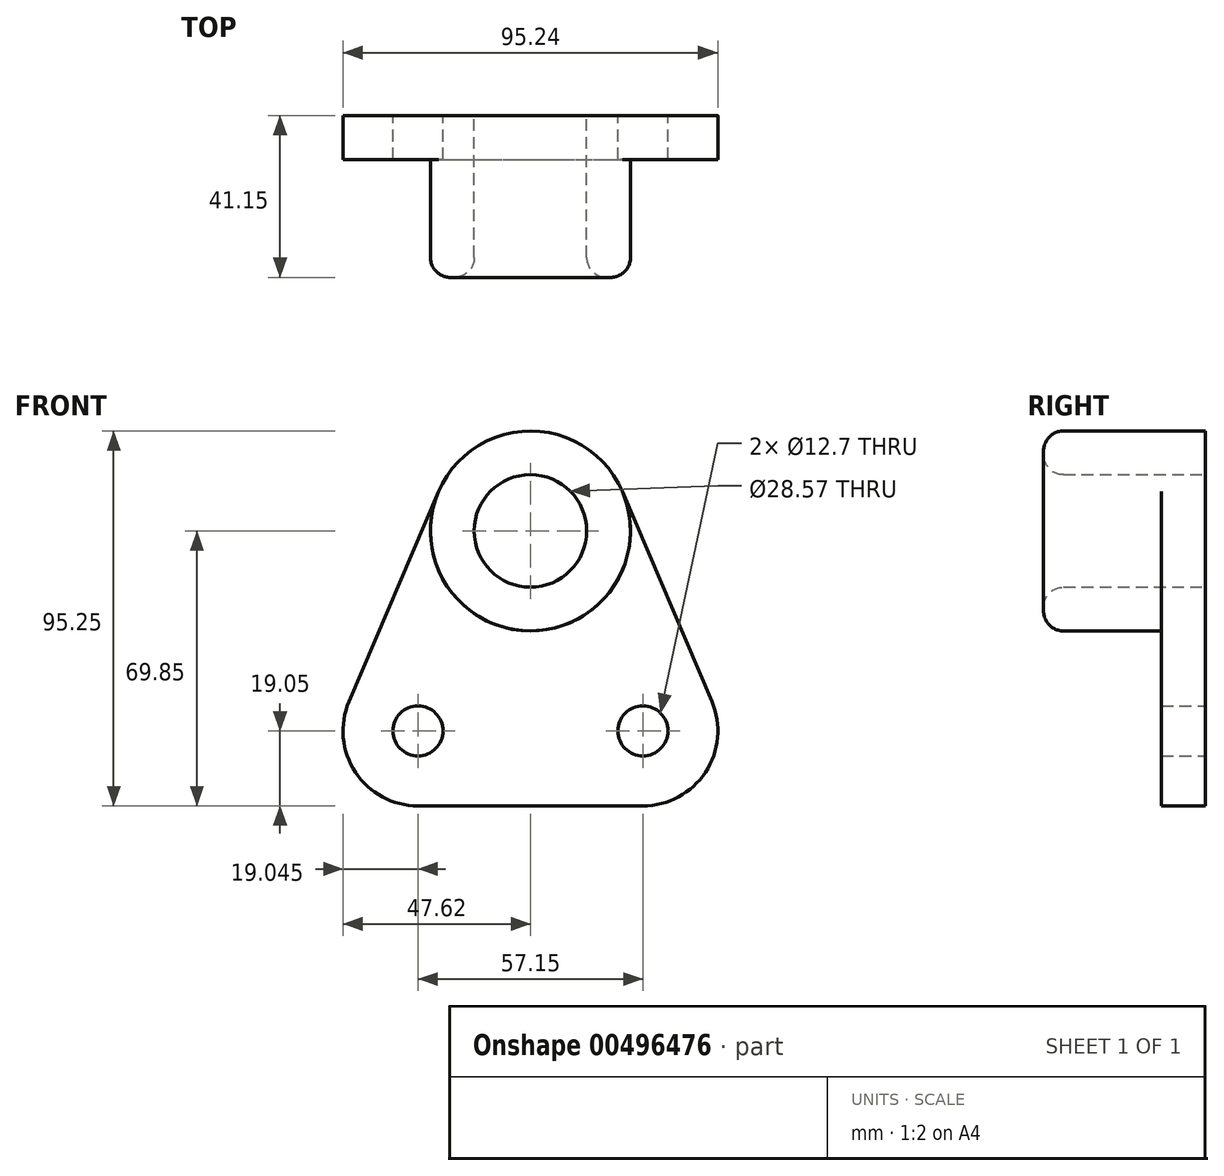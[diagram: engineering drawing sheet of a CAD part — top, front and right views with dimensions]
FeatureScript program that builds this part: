
annotation { "Feature Type Name" : "Feature", "Feature Type Description" : "" }
export const myFeature = defineFeature(function(context is Context, id is Id, definition is map)
    precondition{}
    {
        {
            var Q0;
            Q0=qCreatedBy(makeId("Front.planeOp"),FACE);
            var sketch = newSketch(context, id + "F0", { "sketchPlane" : qUnion([Q0])});
            skCircle(sketch, "E0", {"center": v(0, 0) * mm, "radius": 14.29 * mm});
            skCircle(sketch, "E1", {"center": v(0, 0) * mm, "radius": 25.4 * mm});
            skCircle(sketch, "E2", {"center": v(-28.57, -50.8) * mm, "radius": 19.05 * mm});
            skCircle(sketch, "E3", {"center": v(28.58, -50.8) * mm, "radius": 19.05 * mm});
            skCircle(sketch, "E4", {"center": v(28.58, -50.8) * mm, "radius": 6.35 * mm});
            skCircle(sketch, "E5", {"center": v(-28.57, -50.8) * mm, "radius": 6.35 * mm});
            skLineSegment(sketch, "E6", {"start": v(-23.36, 9.97) * mm, "end": v(-46.1, -43.33) * mm});
            skLineSegment(sketch, "E7", {"start": v(-28.58, -69.85) * mm, "end": v(28.58, -69.85) * mm});
            skLineSegment(sketch, "E8", {"start": v(46.1, -43.33) * mm, "end": v(23.36, 9.97) * mm});
            skLineSegment(sketch, "E9", {"start": v(-28.58, -50.8) * mm, "end": v(0, -50.8) * mm, "construction": true});
            skLineSegment(sketch, "E10", {"start": v(0, -50.8) * mm, "end": v(28.58, -50.8) * mm, "construction": true});
            skSolve(sketch);
        }
        {
            var Q0;
            Q0=makeQuery(id+"F0.imprint","IMPRINT",FACE,{"disambiguationData":[TD([[makeQuery(id+"F0.imprint","IMPRINT",EDGE,{"derivedFrom":sQuery(id+"F0.wireOp",EDGE,"E0")}),-1.0]])]});
            extrude(context, id + "F1", {"entities" : qUnion([Q0]), "depth" : 41.15 * mm, "offsetDistance" : 25.4 * mm});
        }
        {
            var Q0;
            Q0=makeQuery(id+"F1.opExtrude","CAP_FACE",FACE,{"disambiguationData":[OSD([sQuery(id+"F0.wireOp",EDGE,"E0"),sQuery(id+"F0.wireOp",EDGE,"E1")])],"isStart":false});
            fillet(context, id + "F2", {"entities" : qUnion([Q0]), "radius" : 5.08 * mm, "tangentPropagation" : true, "allowEdgeOverflow" : false});
        }
        {
            var Q0;
            {var subQ3=sQuery(id+"F0.wireOp",EDGE,"E6");Q0=makeQuery(id+"F0.imprint","IMPRINT",FACE,{"disambiguationData":[TD([[makeQuery(id+"F0.imprint","IMPRINT",EDGE,{"derivedFrom":subQ3}),1.0]])]});}
            extrude(context, id + "F3", {"entities" : qUnion([Q0]), "operationType" : NewBodyOperationType.ADD, "depth" : 11.18 * mm, "offsetDistance" : 25.4 * mm});
        }
        {
            var Q0;
            Q0=makeQuery(id+"F0.imprint","IMPRINT",FACE,{"disambiguationData":[TD([[makeQuery(id+"F0.imprint","IMPRINT",EDGE,{"derivedFrom":sQuery(id+"F0.wireOp",EDGE,"E5")}),-1.0]])]});
            extrude(context, id + "F4", {"entities" : qUnion([Q0]), "operationType" : NewBodyOperationType.ADD, "depth" : 11.18 * mm, "offsetDistance" : 25.4 * mm});
        }
        {
            var Q0;
            Q0=makeQuery(id+"F0.imprint","IMPRINT",FACE,{"disambiguationData":[TD([[makeQuery(id+"F0.imprint","IMPRINT",EDGE,{"derivedFrom":sQuery(id+"F0.wireOp",EDGE,"E4")}),-1.0]])]});
            extrude(context, id + "F5", {"entities" : qUnion([Q0]), "operationType" : NewBodyOperationType.ADD, "depth" : 11.18 * mm, "offsetDistance" : 25.4 * mm});
        }
    });
